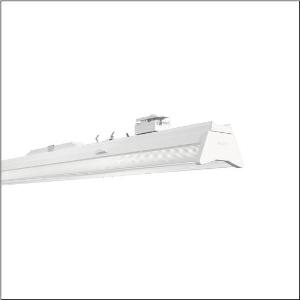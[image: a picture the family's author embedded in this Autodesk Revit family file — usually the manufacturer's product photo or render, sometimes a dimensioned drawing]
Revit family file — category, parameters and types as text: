
# Revit family: licross_11_performance_ho_51td16dn6exmd
name_source: partatom
category: Lighting Fixtures
units: mm (PartAtom-declared; Revit-internal decimal feet)

## family parameters
Cut with Voids When Loaded = No
Host = Face
Light Source = No
Part Type = Normal
Room Calculation Point = No
Round Connector Dimension = Use Diameter
Shared = No

## types (1)
- --- (1 x LED, 2250 lm, 13.9 W, 6500K)
    Apparent Load = 14 VA
    CIE Flux Codes = 63 87 95 78 100
    Color Rendering = 80
    Color Temperature = 6500K
    Default Elevation = 1800 mm
    Description = Licross 11 Performance HO, luminaire insert, of sheet steel, galvanised, coil coated, white, length: 1.500mm, width: 120mm, height: 123mm, LED rated luminous flux: 14.180lm, light colour: 865, SDCM (Standard Deviation of Colour Matching)MacAdam ≤ 2 SDCM (initial), control gear: DALI 2 (for two DALI lines), with plug, 6-pole, with phase selection, mains connection: 220..240V, AC/DC, 0/50..60Hz, rated input power: 81W, internal wiring halogen-free, for central battery installations according to EN 60598-2-22, for emergency light function, without changeover relay, primary light control with lens, of plastic, primary optical cover: cover, of PMMA, light emission: direct/indirect distribution, primary light characteristic: symmetric, protection rating (complete): IP54, insulation class (complete): insulation class I (protective earthing), certification: CE, ENEC, VDE, UKCA, protection symbol: D if used in an environment with non-conductive dust loads with corresponding accessories, impact resistance: IK06, permissible ambient temperature for indoor applications: -25..+35°C, standard: EN 60598-2-22, corresponds to IFS (International Featured Standards) requirements for safety and quality in the food industry, reducing of maximum allowable ambient temperature of 5°C with ceiling mounting, LABS conformity tested according to VDMA 24364:2018-05, The light source and the operating device comply with the requirements of the Ecodesign Regulation (EU) 2019/2020 and are replaceable in accordance with this regulation, packaging unit: 1 piece
    Height = 114 mm
    Lamp = 1 x LED
    Lamp Light Flux = 2250 lm
    Lamp Power = 13.9 W
    Lamp count = 1
    Length = 1500 mm
    Luminous efficacy = 162 lm/W
    Manufacturer = Siteco
    ModVariant = No
    Model = 51TD16DN6EXMD
    Mounting Place = Ceiling
    Mounting Type = Pendant
    Number of Poles = 1
    OnlyDefault = Yes
    Power Factor = 1
    Product Name = Licross 11 Performance HO
    Product group = luminaire insert | ceiling pendant
    ProductGroupID = 901
    Protection Class = Protection class I
    Protection Degree = IP 54
    RLX_Detail_Level = 1
    RLX_Emergency_Light_Flux = 0 lm
    RLX_Emergency_Type = 0
    RLX_Emergency_Type_DB = No
    RlxData = <blob elided: 34913 chars, md5=3d5c328b>
    Socket = socket
    Standby Power = 0 W
    System Light Flux = 2250 lm
    System Power = 14 W
    Type Comments = : DC mode (central or group accumulator) initial emergency light level
    Type Image = l_1256138.jpg
    URL = http://relux.com
    VarID = @adj_057927
    Voltage = 0 V
    Weight = 0.00 kg
    Width = 120 mm

## geometry (parser evidence)
native form markers: Blend x4, Sweep x12
no freeform markers — native parametric forms only
